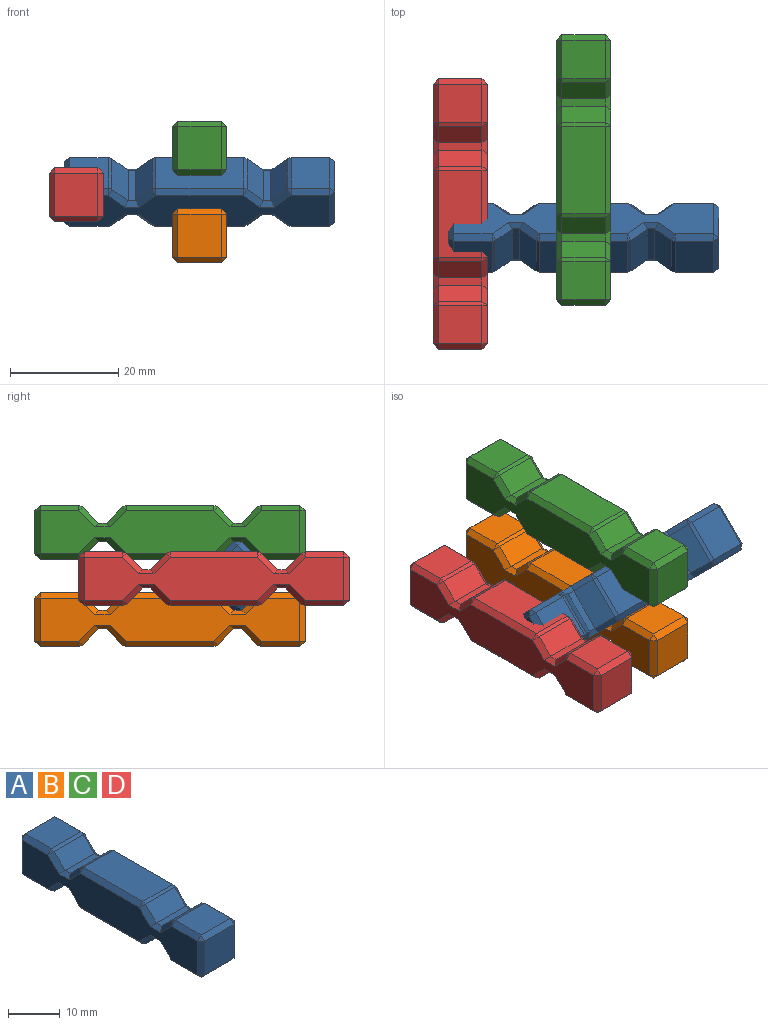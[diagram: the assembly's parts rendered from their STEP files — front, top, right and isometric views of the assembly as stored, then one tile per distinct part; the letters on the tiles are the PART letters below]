
ASSEMBLY  parts=4 mates=2
PART A: 98 faces, bbox 10x50x10 mm
  f0: plane 48x8mm, normal (1,0,0), area 314.1mm2, adj f21,f22,f27,f31,f32,f38,f41,f42
  f1: plane 48x8mm, normal (-1,0,0), area 314.1mm2, adj f24,f25,f30,f34,f35,f39,f44,f45
  f2: plane 8x7.09mm, normal (0,0,1), area 56.7mm2, adj f43,f52,f53,f54
  f3: plane 16.17x8mm, normal (0,0,1), area 129.4mm2, adj f18,f22,f23,f24
  f4: plane 8x7.09mm, normal (0,0,1), area 56.7mm2, adj f36,f41,f45,f46
  f5: plane 16.17x8mm, normal (0,0,-1), area 129.4mm2, adj f86,f91,f94,f97
  f6: plane 8x7.09mm, normal (0,0,-1), area 56.7mm2, adj f56,f61,f65,f66
  f7: plane 8x7.09mm, normal (0,0,-1), area 56.7mm2, adj f63,f72,f73,f74
  f8: plane 8x8mm, normal (0,-1,0), area 64mm2, adj f46,f51,f55,f56
  f9: plane 8x8mm, normal (0,1,0), area 64mm2, adj f53,f62,f63,f64
  f10: plane 8x3mm, normal (0,-0.71,-0.71), area 33.9mm2, adj f73,f82,f83,f84
  f11: plane 8x3mm, normal (0,0.71,-0.71), area 33.9mm2, adj f83,f92,f93,f97
  f12: plane 8x3mm, normal (0,-0.71,-0.71), area 33.9mm2, adj f76,f81,f85,f86
  f13: plane 8x3mm, normal (0,0.71,-0.71), area 33.9mm2, adj f66,f71,f75,f76
  f14: plane 8x3mm, normal (0,0.71,0.71), area 33.9mm2, adj f26,f31,f35,f36
  f15: plane 8x3mm, normal (0,-0.71,0.71), area 33.9mm2, adj f18,f21,f25,f26
  f16: plane 8x3mm, normal (0,-0.71,0.71), area 33.9mm2, adj f33,f42,f43,f44
  f17: plane 8x3mm, normal (0,0.71,0.71), area 33.9mm2, adj f23,f32,f33,f34
  f18: plane 8x0.71mm, normal (0,-0.38,0.92), area 6.1mm2, adj f3,f15,f19,f20
  f19: plane 1x1mm, normal (0.68,-0.28,0.68), area 0.5mm2, adj f18,f21,f22
  f20: plane 1x1mm, normal (-0.68,-0.28,0.68), area 0.5mm2, adj f18,f24,f25
  f21: plane 3.71x3.71mm, normal (0.71,-0.5,0.5), area 6mm2, adj f0,f15,f19,f27
  f22: plane 16.17x1mm, normal (0.71,0,0.71), area 22.9mm2, adj f0,f3,f19,f28
  f23: plane 8x0.71mm, normal (0,0.38,0.92), area 6.1mm2, adj f3,f17,f28,f29
  f24: plane 16.17x1mm, normal (-0.71,0,0.71), area 22.9mm2, adj f1,f3,f20,f29
  f25: plane 3.71x3.71mm, normal (-0.71,-0.5,0.5), area 6mm2, adj f1,f15,f20,f30
  f26: plane 8x1.41mm, normal (0,0,1), area 11.3mm2, adj f14,f15,f27,f30
  f27: plane 2.83x1mm, normal (0.58,0,0.82), area 2.6mm2, adj f0,f21,f26,f31
  f28: plane 1x1mm, normal (0.68,0.28,0.68), area 0.5mm2, adj f22,f23,f32
  f29: plane 1x1mm, normal (-0.68,0.28,0.68), area 0.5mm2, adj f23,f24,f34
  f30: plane 2.83x1mm, normal (-0.58,0,0.82), area 2.6mm2, adj f1,f25,f26,f35
  f31: plane 3.71x3.71mm, normal (0.71,0.5,0.5), area 6mm2, adj f0,f14,f27,f37
  f32: plane 3.71x3.71mm, normal (0.71,0.5,0.5), area 6mm2, adj f0,f17,f28,f38
  f33: plane 8x1.41mm, normal (0,0,1), area 11.3mm2, adj f16,f17,f38,f39
  f34: plane 3.71x3.71mm, normal (-0.71,0.5,0.5), area 6mm2, adj f1,f17,f29,f39
  f35: plane 3.71x3.71mm, normal (-0.71,0.5,0.5), area 6mm2, adj f1,f14,f30,f40
  f36: plane 8x0.71mm, normal (0,0.38,0.92), area 6.1mm2, adj f4,f14,f37,f40
  f37: plane 1x1mm, normal (0.68,0.28,0.68), area 0.5mm2, adj f31,f36,f41
  f38: plane 2.83x1mm, normal (0.58,0,0.82), area 2.6mm2, adj f0,f32,f33,f42
  f39: plane 2.83x1mm, normal (-0.58,0,0.82), area 2.6mm2, adj f1,f33,f34,f44
  f40: plane 1x1mm, normal (-0.68,0.28,0.68), area 0.5mm2, adj f35,f36,f45
  f41: plane 7.09x1mm, normal (0.71,0,0.71), area 10mm2, adj f0,f4,f37,f47
  f42: plane 3.71x3.71mm, normal (0.71,-0.5,0.5), area 6mm2, adj f0,f16,f38,f48
  f43: plane 8x0.71mm, normal (0,-0.38,0.92), area 6.1mm2, adj f2,f16,f48,f49
  f44: plane 3.71x3.71mm, normal (-0.71,-0.5,0.5), area 6mm2, adj f1,f16,f39,f49
  f45: plane 7.09x1mm, normal (-0.71,0,0.71), area 10mm2, adj f1,f4,f40,f50
  f46: plane 8x1mm, normal (0,-0.71,0.71), area 11.3mm2, adj f4,f8,f47,f50
  f47: plane 1x1mm, normal (0.58,-0.58,0.58), area 0.9mm2, adj f41,f46,f51
  f48: plane 1x1mm, normal (0.68,-0.28,0.68), area 0.5mm2, adj f42,f43,f52
  f49: plane 1x1mm, normal (-0.68,-0.28,0.68), area 0.5mm2, adj f43,f44,f54
  f50: plane 1x1mm, normal (-0.58,-0.58,0.58), area 0.9mm2, adj f45,f46,f55
  f51: plane 8x1mm, normal (0.71,-0.71,0), area 11.3mm2, adj f0,f8,f47,f57
  f52: plane 7.09x1mm, normal (0.71,0,0.71), area 10mm2, adj f0,f2,f48,f58
  f53: plane 8x1mm, normal (0,0.71,0.71), area 11.3mm2, adj f2,f9,f58,f59
  f54: plane 7.09x1mm, normal (-0.71,0,0.71), area 10mm2, adj f1,f2,f49,f59
  f55: plane 8x1mm, normal (-0.71,-0.71,0), area 11.3mm2, adj f1,f8,f50,f60
  f56: plane 8x1mm, normal (0,-0.71,-0.71), area 11.3mm2, adj f6,f8,f57,f60
  f57: plane 1x1mm, normal (0.58,-0.58,-0.58), area 0.9mm2, adj f51,f56,f61
  f58: plane 1x1mm, normal (0.58,0.58,0.58), area 0.9mm2, adj f52,f53,f62
  f59: plane 1x1mm, normal (-0.58,0.58,0.58), area 0.9mm2, adj f53,f54,f64
  f60: plane 1x1mm, normal (-0.58,-0.58,-0.58), area 0.9mm2, adj f55,f56,f65
  f61: plane 7.09x1mm, normal (0.71,0,-0.71), area 10mm2, adj f0,f6,f57,f67
  f62: plane 8x1mm, normal (0.71,0.71,0), area 11.3mm2, adj f0,f9,f58,f68
  f63: plane 8x1mm, normal (0,0.71,-0.71), area 11.3mm2, adj f7,f9,f68,f69
  f64: plane 8x1mm, normal (-0.71,0.71,0), area 11.3mm2, adj f1,f9,f59,f69
  f65: plane 7.09x1mm, normal (-0.71,0,-0.71), area 10mm2, adj f1,f6,f60,f70
  f66: plane 8x0.71mm, normal (0,0.38,-0.92), area 6.1mm2, adj f6,f13,f67,f70
  f67: plane 1x1mm, normal (0.68,0.28,-0.68), area 0.5mm2, adj f61,f66,f71
  f68: plane 1x1mm, normal (0.58,0.58,-0.58), area 0.9mm2, adj f62,f63,f72
  f69: plane 1x1mm, normal (-0.58,0.58,-0.58), area 0.9mm2, adj f63,f64,f74
  f70: plane 1x1mm, normal (-0.68,0.28,-0.68), area 0.5mm2, adj f65,f66,f75
  f71: plane 3.71x3.71mm, normal (0.71,0.5,-0.5), area 6mm2, adj f0,f13,f67,f77
  f72: plane 7.09x1mm, normal (0.71,0,-0.71), area 10mm2, adj f0,f7,f68,f78
  f73: plane 8x0.71mm, normal (0,-0.38,-0.92), area 6.1mm2, adj f7,f10,f78,f79
  f74: plane 7.09x1mm, normal (-0.71,0,-0.71), area 10mm2, adj f1,f7,f69,f79
  f75: plane 3.71x3.71mm, normal (-0.71,0.5,-0.5), area 6mm2, adj f1,f13,f70,f80
  f76: plane 8x1.41mm, normal (0,0,-1), area 11.3mm2, adj f12,f13,f77,f80
  f77: plane 2.83x1mm, normal (0.58,0,-0.82), area 2.6mm2, adj f0,f71,f76,f81
  f78: plane 1x1mm, normal (0.68,-0.28,-0.68), area 0.5mm2, adj f72,f73,f82
  f79: plane 1x1mm, normal (-0.68,-0.28,-0.68), area 0.5mm2, adj f73,f74,f84
  f80: plane 2.83x1mm, normal (-0.58,0,-0.82), area 2.6mm2, adj f1,f75,f76,f85
  f81: plane 3.71x3.71mm, normal (0.71,-0.5,-0.5), area 6mm2, adj f0,f12,f77,f87
  f82: plane 3.71x3.71mm, normal (0.71,-0.5,-0.5), area 6mm2, adj f0,f10,f78,f88
  f83: plane 8x1.41mm, normal (0,0,-1), area 11.3mm2, adj f10,f11,f88,f89
  f84: plane 3.71x3.71mm, normal (-0.71,-0.5,-0.5), area 6mm2, adj f1,f10,f79,f89
  f85: plane 3.71x3.71mm, normal (-0.71,-0.5,-0.5), area 6mm2, adj f1,f12,f80,f90
  f86: plane 8x0.71mm, normal (0,-0.38,-0.92), area 6.1mm2, adj f5,f12,f87,f90
  f87: plane 1x1mm, normal (0.68,-0.28,-0.68), area 0.5mm2, adj f81,f86,f91
  f88: plane 2.83x1mm, normal (0.58,0,-0.82), area 2.6mm2, adj f0,f82,f83,f92
  f89: plane 2.83x1mm, normal (-0.58,0,-0.82), area 2.6mm2, adj f1,f83,f84,f93
  f90: plane 1x1mm, normal (-0.68,-0.28,-0.68), area 0.5mm2, adj f85,f86,f94
  f91: plane 16.17x1mm, normal (0.71,0,-0.71), area 22.9mm2, adj f0,f5,f87,f95
  f92: plane 3.71x3.71mm, normal (0.71,0.5,-0.5), area 6mm2, adj f0,f11,f88,f95
  f93: plane 3.71x3.71mm, normal (-0.71,0.5,-0.5), area 6mm2, adj f1,f11,f89,f96
  f94: plane 16.17x1mm, normal (-0.71,0,-0.71), area 22.9mm2, adj f1,f5,f90,f96
  f95: plane 1x1mm, normal (0.68,0.28,-0.68), area 0.5mm2, adj f91,f92,f97
  f96: plane 1x1mm, normal (-0.68,0.28,-0.68), area 0.5mm2, adj f93,f94,f97
  f97: plane 8x0.71mm, normal (0,0.38,-0.92), area 6.1mm2, adj f5,f11,f95,f96
PART B: same geometry as A
PART C: same geometry as A
PART D: same geometry as A
PLACE A rot(axis=(-0.68,0.68,0.28),148.6deg) t=(3.69,-12.34,5.12)mm
PLACE B t=(3.69,0.16,-2.95)mm fixed
PLACE C rot(axis=(-1,0,0),180deg) t=(3.69,0.16,13.19)mm
PLACE D t=(-19.11,-7.96,4.61)mm
MATE fastened C.f17 <-> A.f1  axis (0,-0.71,-0.71) through (3.69,-11.63,11.49)mm
MATE planar B.f15 <-> A.f3  axis (0,-0.71,0.71) through (3.69,-11.63,-1.24)mm
